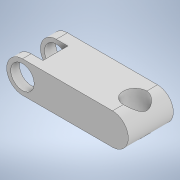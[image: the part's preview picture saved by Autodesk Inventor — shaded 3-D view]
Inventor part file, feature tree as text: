
AUTODESK INVENTOR PART (.ipt)
format: ipt  version: 2022 (Build 260153000, 153)  size: 135,680 bytes
history: native  units: in
note: dims shown in document units (in); Inventor stores cm internally (conversion verified against a paired STEP export)
features: extrude x3, sketch x3
ambient origin geometry x8: Origin, YZ Plane, XZ Plane, XY Plane, X Axis, Y Axis, Z Axis, Center Point
bodies: Solid1 (feature_tree)
feature tree (6):
  extrude  "Extrusion1"  Depth=0.7in
  extrude  "Extrusion2"  Depth=2.0in TaperAngle=0.0deg
  extrude  "Extrusion3"  Depth=0.52in
  sketch  "Sketch1"  dims[d0=0.52in d1=0.7in]
  sketch  "Sketch2"  dims[d2=2.0in d4=1.0in d5=0.0in]
  sketch  "Sketch3"  dims[d6=1.0in d7=0.0in d8=0.52in d9=1.0in d10=0.0in]
